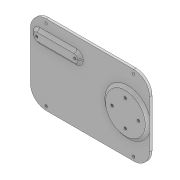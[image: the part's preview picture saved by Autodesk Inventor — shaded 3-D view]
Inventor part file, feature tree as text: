
AUTODESK INVENTOR PART (.ipt)
format: ipt  version: 2022 (Build 260153000, 153)  size: 278,528 bytes
history: native  units: mm
features: extrude x6, sketch x6, projected_geometry x5, fillet x3, other x1
ambient origin geometry x8: Origin, YZ Plane, XZ Plane, XY Plane, X Axis, Y Axis, Z Axis, Center Point
bodies: Body1 (feature_tree)
feature tree (21):
  other  "Sólido1"
  extrude  "Extrusión1"  Depth=100.0mm
  extrude  "Extrusión2"  Depth=3.0mm
  fillet  "Empalme1"  Radius=16.5mm
  extrude  "Extrusión3"  Depth=16.5mm
  fillet  "Empalme2"  Radius=2.2mm
  fillet  "Empalme3"  Radius=2.2mm
  extrude  "Extrusión4"  Depth=2.2mm
  extrude  "Extrusión5"  Depth=10.0mm
  extrude  "Extrusión6"  Depth=5.0mm
  sketch  "Boceto1"  dims[d0=150.0mm d1=100.0mm]
  sketch  "Boceto2"  dims[d2=3.0mm d3=0.0mm d4=33.0mm d5=16.5mm]
  projected_geometry  "Contorno proyectado1"
  sketch  "Boceto3"  dims[d6=33.0mm d7=16.5mm d8=2.2mm d9=2.2mm]
  projected_geometry  "Contorno proyectado2"
  sketch  "Boceto4"  dims[d10=2.2mm d11=2.2mm]
  projected_geometry  "Contorno proyectado3"
  sketch  "Boceto5"  dims[d13=10.0mm d14=0.0mm d15=48.0mm]
  projected_geometry  "Contorno proyectado4"
  sketch  "Boceto6"  dims[d16=24.0mm d17=47.0mm d18=27.8mm d19=2.2mm d20=2.2mm d21=20.0mm d22=128.0mm d24=64.0mm d25=50.0mm d26=10.0mm d27=55.0mm d28=27.5mm d29=5.0mm d30=3.0mm d31=0.0mm d32=4.0mm d33=4.0mm d34=3.8mm d35=3.8mm d36=3.8mm d37=3.8mm d38=3.8mm d39=3.8mm d40=5.0mm d41=0.0mm d42=3.2mm d43=3.2mm d44=3.2mm d45=3.2mm d46=3.2mm d47=3.2mm d48=0.0mm d49=0.0mm d50=20.0mm d51=5.0mm d52=20.0mm d53=5.0mm d54=3.2mm d55=3.2mm d56=3.2mm d57=3.2mm d58=0.0mm d59=0.0mm]
  projected_geometry  "Contorno proyectado5"
